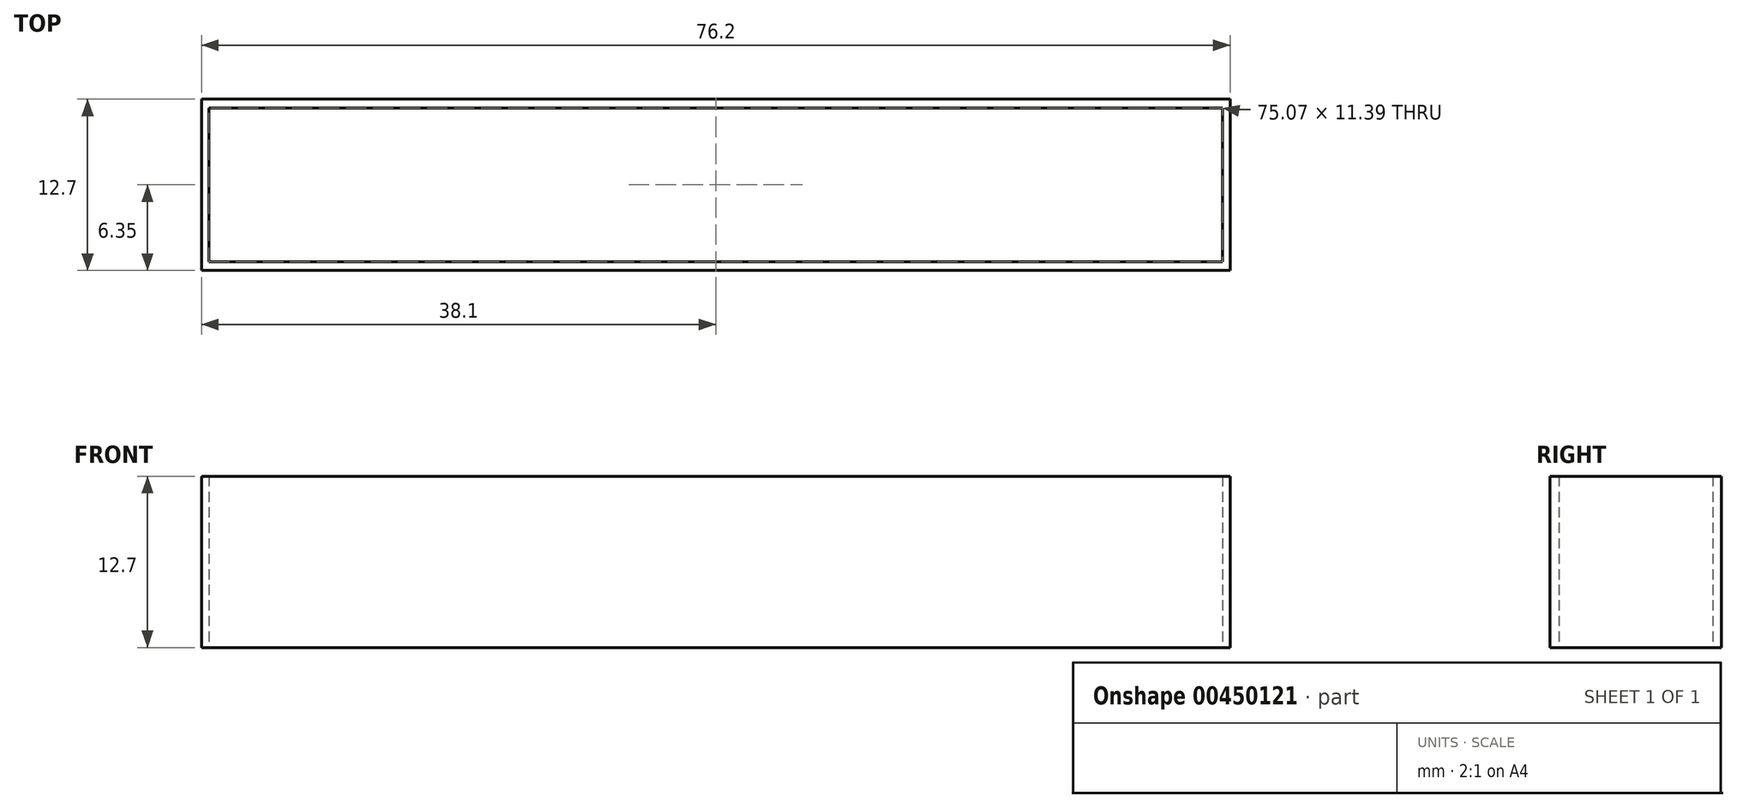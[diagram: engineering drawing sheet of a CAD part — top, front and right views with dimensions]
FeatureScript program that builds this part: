
annotation { "Feature Type Name" : "Feature", "Feature Type Description" : "" }
export const myFeature = defineFeature(function(context is Context, id is Id, definition is map)
    precondition{}
    {
        {
            var Q0;
            Q0=qCreatedBy(makeId("Top.planeOp"),FACE);
            var sketch = newSketch(context, id + "F0", { "sketchPlane" : qUnion([Q0])});
            skLineSegment(sketch, "E0.bottom", {"start": v(-38.1, 6.35) * mm, "end": v(38.1, 6.35) * mm});
            skLineSegment(sketch, "E0.top", {"start": v(-38.1, -6.35) * mm, "end": v(38.1, -6.35) * mm});
            skLineSegment(sketch, "E0.left", {"start": v(-38.1, 6.35) * mm, "end": v(-38.1, -6.35) * mm});
            skLineSegment(sketch, "E0.right", {"start": v(38.1, 6.35) * mm, "end": v(38.1, -6.35) * mm});
            skPoint(sketch, "E0.middle", {"position": v(0, 0) * mm});
            skLineSegment(sketch, "E1.bottom", {"start": v(-37.53, 5.7) * mm, "end": v(37.53, 5.7) * mm});
            skLineSegment(sketch, "E1.top", {"start": v(-37.53, -5.7) * mm, "end": v(37.53, -5.7) * mm});
            skLineSegment(sketch, "E1.left", {"start": v(-37.53, 5.7) * mm, "end": v(-37.53, -5.7) * mm});
            skLineSegment(sketch, "E1.right", {"start": v(37.53, 5.7) * mm, "end": v(37.53, -5.7) * mm});
            skLineSegment(sketch, "E2.bottom", {"start": v(-36.9, 5.08) * mm, "end": v(36.9, 5.08) * mm});
            skLineSegment(sketch, "E2.top", {"start": v(-36.9, -5.08) * mm, "end": v(36.9, -5.08) * mm});
            skLineSegment(sketch, "E2.left", {"start": v(-36.9, 5.08) * mm, "end": v(-36.9, -5.08) * mm});
            skLineSegment(sketch, "E2.right", {"start": v(36.9, 5.08) * mm, "end": v(36.9, -5.08) * mm});
            skSolve(sketch);
        }
        {
            var Q0;
            Q0 = qSketchRegion(id + "F0", true);
            extrude(context, id + "F1", {"entities" : qUnion([Q0]), "depth" : 12.7 * mm});
        }
    });
